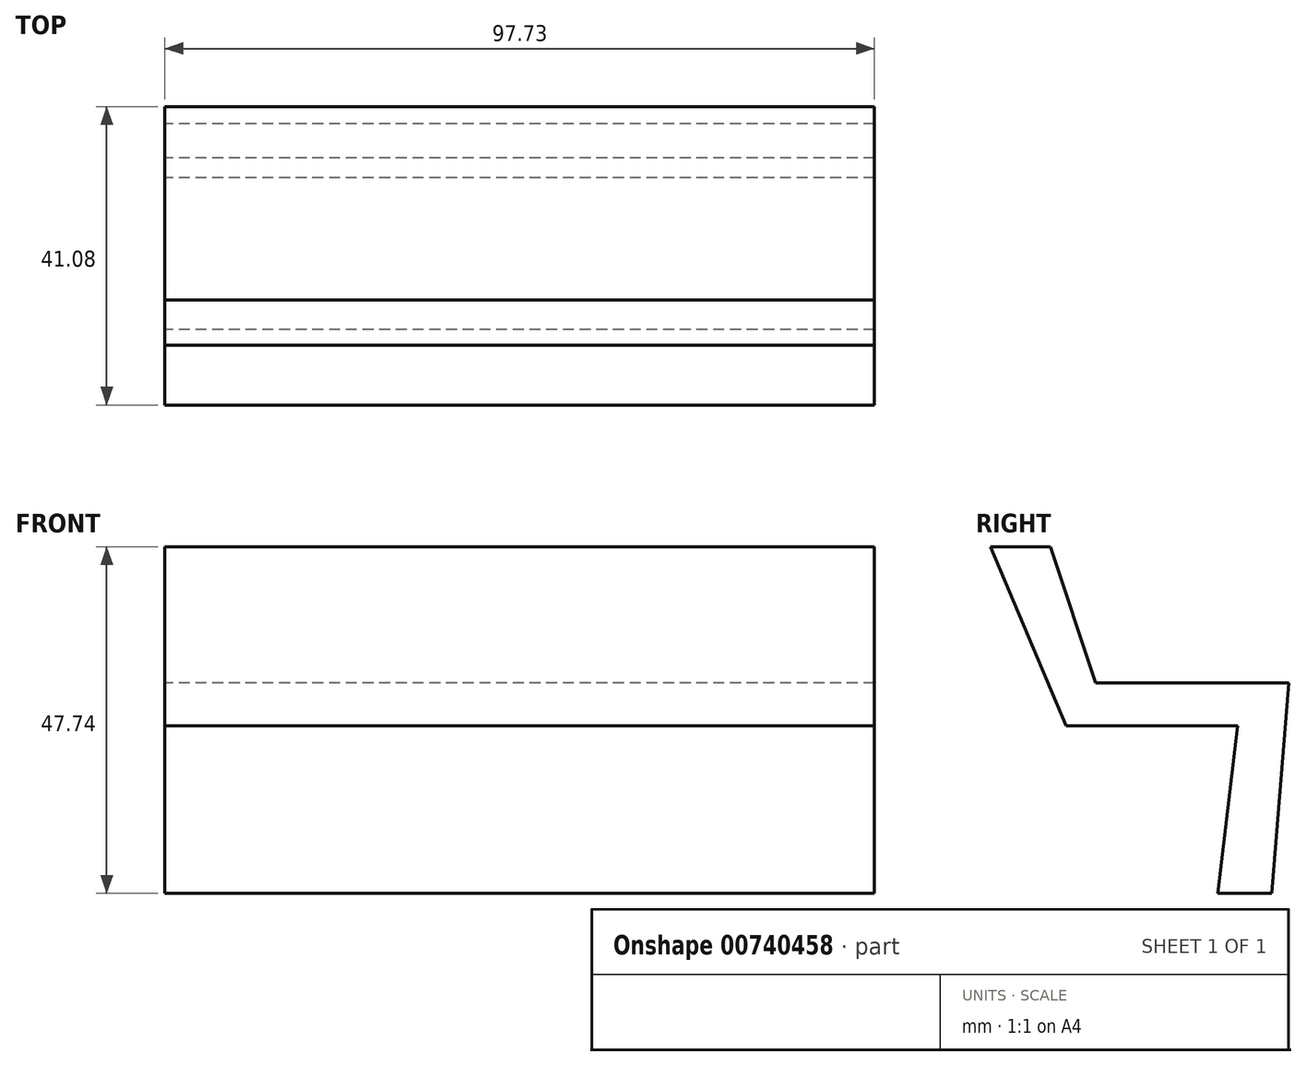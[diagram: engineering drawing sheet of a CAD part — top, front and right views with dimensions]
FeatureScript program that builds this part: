
annotation { "Feature Type Name" : "Feature", "Feature Type Description" : "" }
export const myFeature = defineFeature(function(context is Context, id is Id, definition is map)
    precondition{}
    {
        {
            var Q0;
            Q0=qCreatedBy(makeId("Right.planeOp"),FACE);
            var sketch = newSketch(context, id + "F0", { "sketchPlane" : qUnion([Q0])});
            skLineSegment(sketch, "E0", {"start": v(18.68, 0) * mm, "end": v(11.25, 0) * mm});
            skLineSegment(sketch, "E1", {"start": v(11.25, 0) * mm, "end": v(13.99, 23.09) * mm});
            skLineSegment(sketch, "E2", {"start": v(13.99, 23.09) * mm, "end": v(-9.68, 23.09) * mm});
            skLineSegment(sketch, "E3", {"start": v(-9.68, 23.09) * mm, "end": v(-20.05, 47.74) * mm});
            skLineSegment(sketch, "E4", {"start": v(-20.05, 47.74) * mm, "end": v(-11.84, 47.74) * mm});
            skLineSegment(sketch, "E5", {"start": v(-11.84, 47.74) * mm, "end": v(-5.58, 28.96) * mm});
            skLineSegment(sketch, "E6", {"start": v(-5.58, 28.96) * mm, "end": v(21.03, 28.96) * mm});
            skLineSegment(sketch, "E7", {"start": v(21.03, 28.96) * mm, "end": v(18.68, 0) * mm});
            skSolve(sketch);
        }
        {
            var Q0;
            Q0=qCreatedBy(makeId("Front.planeOp"),FACE);
            var sketch = newSketch(context, id + "F1", { "sketchPlane" : qUnion([Q0])});
            skLineSegment(sketch, "E8", {"start": v(0, 48.13) * mm, "end": v(-97.73, 48.13) * mm});
            skSolve(sketch);
        }
        {
            var Q0;
            Q0=makeQuery(id+"F0.imprint","IMPRINT",FACE,{"disambiguationData":[TD([[makeQuery(id+"F0.imprint","IMPRINT",EDGE,{"derivedFrom":sQuery(id+"F0.wireOp",EDGE,"E0")}),-1.0]])]});
            var Q1;
            Q1=sQuery(id+"F1.wireOp",EDGE,"E8");
            sweep(context, id + "F2", {"profiles" : qUnion([Q0]), "path" : qUnion([Q1])});
        }
    });
